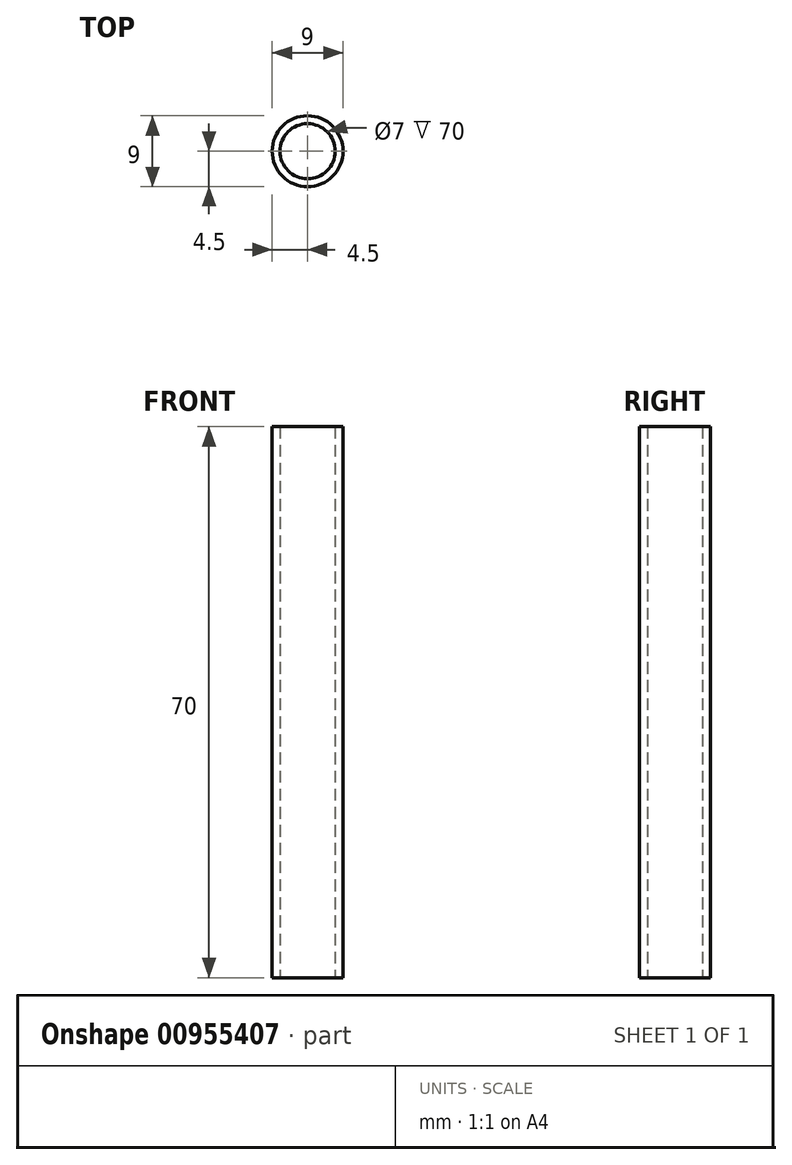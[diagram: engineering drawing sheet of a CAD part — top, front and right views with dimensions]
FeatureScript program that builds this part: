
annotation { "Feature Type Name" : "Feature", "Feature Type Description" : "" }
export const myFeature = defineFeature(function(context is Context, id is Id, definition is map)
    precondition{}
    {
        {
            var Q0;
            Q0=qCreatedBy(makeId("Top.planeOp"),FACE);
            var sketch = newSketch(context, id + "F0", { "sketchPlane" : qUnion([Q0])});
            skCircle(sketch, "E0", {"center": v(0, 0) * mm, "radius": 3.5 * mm});
            skCircle(sketch, "E1", {"center": v(0, 0) * mm, "radius": 4.5 * mm});
            skSolve(sketch);
        }
        {
            var Q0;
            Q0 = qSketchRegion(id + "F0", true);
            extrude(context, id + "F1", {"entities" : qUnion([Q0]), "depth" : 70 * mm, "offsetDistance" : 25 * mm});
        }
    });
